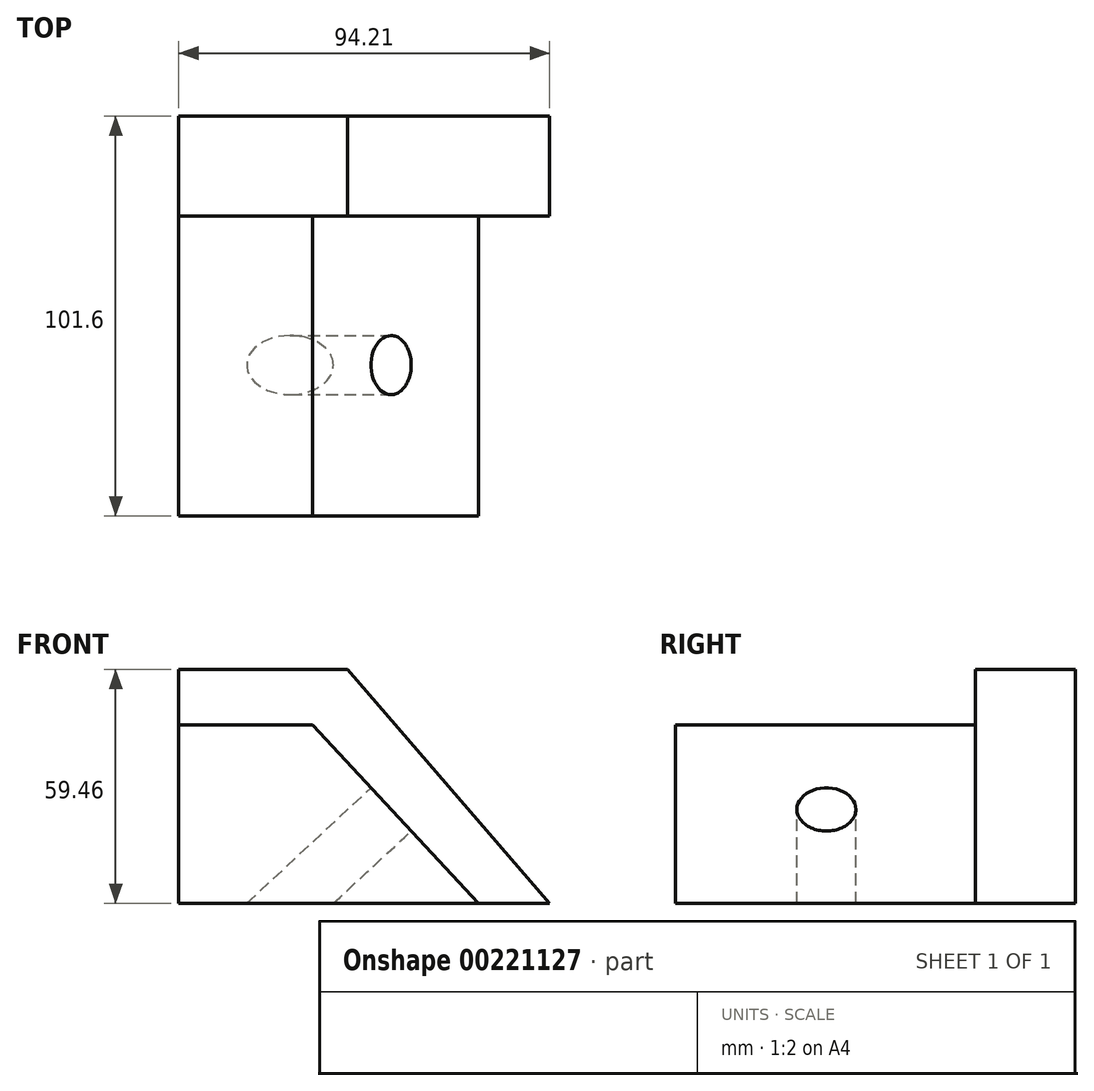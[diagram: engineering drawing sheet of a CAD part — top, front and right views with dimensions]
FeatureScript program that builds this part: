
annotation { "Feature Type Name" : "Feature", "Feature Type Description" : "" }
export const myFeature = defineFeature(function(context is Context, id is Id, definition is map)
    precondition{}
    {
        {
            var Q0;
            Q0=qCreatedBy(makeId("Front.planeOp"),FACE);
            var sketch = newSketch(context, id + "F0", { "sketchPlane" : qUnion([Q0])});
            skLineSegment(sketch, "E0.bottom", {"start": v(-76.2, 45.37) * mm, "end": v(0, 45.37) * mm});
            skLineSegment(sketch, "E0.top", {"start": v(-76.2, 0) * mm, "end": v(0, 0) * mm});
            skLineSegment(sketch, "E0.left", {"start": v(-76.2, 45.37) * mm, "end": v(-76.2, 0) * mm});
            skLineSegment(sketch, "E0.right", {"start": v(0, 45.37) * mm, "end": v(0, 0) * mm});
            skSolve(sketch);
        }
        {
            var Q0;
            Q0 = qSketchRegion(id + "F0", true);
            extrude(context, id + "F1", {"entities" : qUnion([Q0]), "depth" : 76.2 * mm});
        }
        {
            var Q0;
            Q0=makeQuery(id+"F1.opExtrude","CAP_FACE",FACE,{"disambiguationData":[OSD([sQuery(id+"F0.wireOp",EDGE,"E0.bottom"),sQuery(id+"F0.wireOp",EDGE,"E0.top"),sQuery(id+"F0.wireOp",EDGE,"E0.left"),sQuery(id+"F0.wireOp",EDGE,"E0.right")])],"isStart":false});
            var sketch = newSketch(context, id + "F2", { "sketchPlane" : qUnion([Q0])});
            skLineSegment(sketch, "E1", {"start": v(-42.26, 45.37) * mm, "end": v(0, 0) * mm});
            skLineSegment(sketch, "E2", {"start": v(0, 0) * mm, "end": v(0, 45.37) * mm});
            skLineSegment(sketch, "E3", {"start": v(0, 45.37) * mm, "end": v(-42.26, 45.37) * mm});
            skSolve(sketch);
        }
        {
            var Q0;
            Q0 = qSketchRegion(id + "F2", true);
            extrude(context, id + "F3", {"entities" : qUnion([Q0]), "operationType" : NewBodyOperationType.REMOVE, "endBound" : BoundingType.THROUGH_ALL, "oppositeDirection" : true, "depth" : 76.2 * mm});
        }
        {
            var Q0;
            Q0=makeQuery(id+"F3.boolean.opBoolean","COPY",FACE,{"derivedFrom":makeQuery(id+"F3.opExtrude","SWEPT_FACE",FACE,{"disambiguationData":[OSD([sQuery(id+"F2.wireOp",EDGE,"E1")])]})});
            var sketch = newSketch(context, id + "F4", { "sketchPlane" : qUnion([Q0])});
            skCircle(sketch, "E4", {"center": v(-37.87, 32.66) * mm, "radius": 7.5 * mm});
            skSolve(sketch);
        }
        {
            var Q0;
            Q0 = qSketchRegion(id + "F4", true);
            extrude(context, id + "F5", {"entities" : qUnion([Q0]), "operationType" : NewBodyOperationType.REMOVE, "endBound" : BoundingType.THROUGH_ALL, "oppositeDirection" : true, "depth" : 25.4 * mm});
        }
        {
            var Q0;
            Q0=makeQuery(id+"F1.opExtrude","CAP_FACE",FACE,{"disambiguationData":[OSD([sQuery(id+"F0.wireOp",EDGE,"E0.bottom"),sQuery(id+"F0.wireOp",EDGE,"E0.top"),sQuery(id+"F0.wireOp",EDGE,"E0.left"),sQuery(id+"F0.wireOp",EDGE,"E0.right")])],"isStart":true});
            var sketch = newSketch(context, id + "F6", { "sketchPlane" : qUnion([Q0])});
            skLineSegment(sketch, "E5.bottom", {"start": v(-18.01, 0) * mm, "end": v(76.2, 0) * mm});
            skLineSegment(sketch, "E5.top", {"start": v(-18.01, 59.46) * mm, "end": v(76.2, 59.46) * mm});
            skLineSegment(sketch, "E5.left", {"start": v(-18.01, 0) * mm, "end": v(-18.01, 59.46) * mm});
            skLineSegment(sketch, "E5.right", {"start": v(76.2, 0) * mm, "end": v(76.2, 59.46) * mm});
            skSolve(sketch);
        }
        {
            var Q0;
            Q0 = qSketchRegion(id + "F6", true);
            extrude(context, id + "F7", {"entities" : qUnion([Q0]), "operationType" : NewBodyOperationType.ADD, "depth" : 25.4 * mm});
        }
        {
            var Q0;
            Q0=makeQuery(id+"F7.opExtrude","CAP_FACE",FACE,{"disambiguationData":[OSD([sQuery(id+"F6.wireOp",EDGE,"E5.bottom"),sQuery(id+"F6.wireOp",EDGE,"E5.top"),sQuery(id+"F6.wireOp",EDGE,"E5.left"),sQuery(id+"F6.wireOp",EDGE,"E5.right")])],"isStart":false});
            var sketch = newSketch(context, id + "F8", { "sketchPlane" : qUnion([Q0])});
            skLineSegment(sketch, "E6", {"start": v(-18.01, 0) * mm, "end": v(33.3, 59.46) * mm});
            skLineSegment(sketch, "E7", {"start": v(33.3, 59.46) * mm, "end": v(-18.01, 59.46) * mm});
            skLineSegment(sketch, "E8", {"start": v(-18.01, 59.46) * mm, "end": v(-18.01, 0) * mm});
            skSolve(sketch);
        }
        {
            var Q0;
            Q0 = qSketchRegion(id + "F8", true);
            extrude(context, id + "F9", {"entities" : qUnion([Q0]), "operationType" : NewBodyOperationType.REMOVE, "endBound" : BoundingType.THROUGH_ALL, "oppositeDirection" : true, "depth" : 25.4 * mm});
        }
    });
